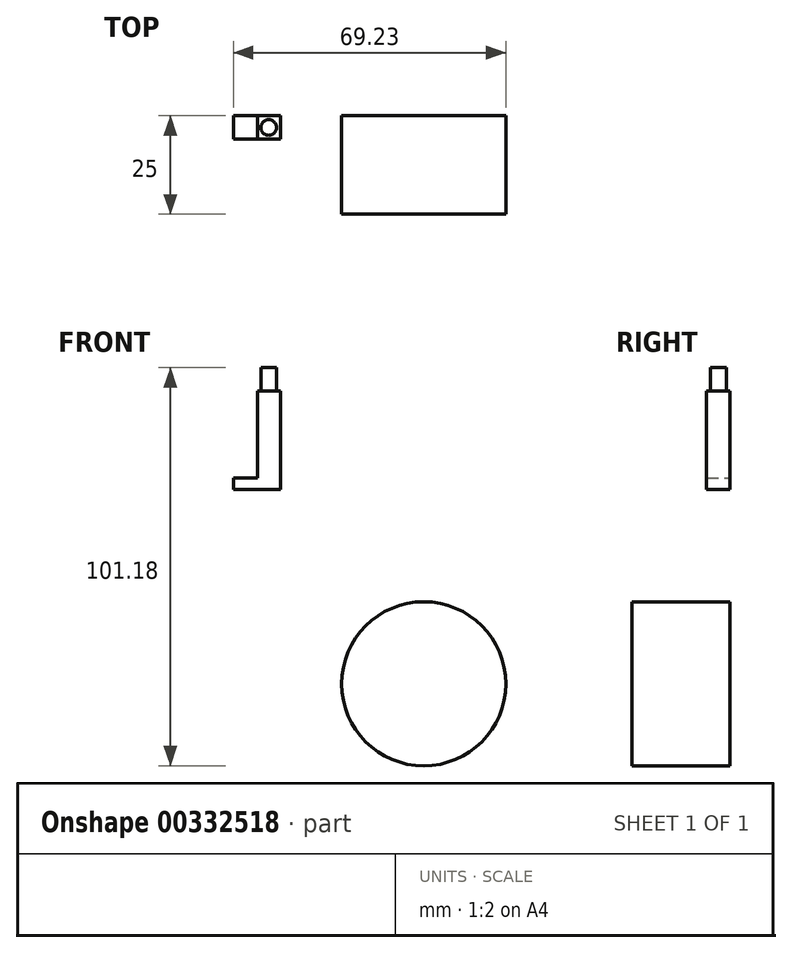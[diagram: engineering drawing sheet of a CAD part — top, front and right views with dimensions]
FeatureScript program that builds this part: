
annotation { "Feature Type Name" : "Feature", "Feature Type Description" : "" }
export const myFeature = defineFeature(function(context is Context, id is Id, definition is map)
    precondition{}
    {
        {
            var Q0;
            Q0=qCreatedBy(makeId("Front.planeOp"),FACE);
            var sketch = newSketch(context, id + "F0", { "sketchPlane" : qUnion([Q0])});
            skCircle(sketch, "E0", {"center": v(0, 0) * mm, "radius": 20.84 * mm});
            skSolve(sketch);
        }
        {
            var Q0;
            Q0 = qSketchRegion(id + "F0", true);
            extrude(context, id + "F1", {"entities" : qUnion([Q0]), "depth" : 25 * mm});
        }
        {
            var Q0;
            Q0=qCreatedBy(makeId("Front.planeOp"),FACE);
            var sketch = newSketch(context, id + "F2", { "sketchPlane" : qUnion([Q0])});
            skLineSegment(sketch, "E1", {"start": v(-47.44, 33.57) * mm, "end": v(-47.44, 31.07) * mm});
            skLineSegment(sketch, "E2", {"start": v(-47.44, 31.07) * mm, "end": v(3.32, 13.52) * mm});
            skLineSegment(sketch, "E3", {"start": v(-36.39, 74.34) * mm, "end": v(-36.39, 49.34) * mm});
            skLineSegment(sketch, "E4", {"start": v(-36.39, 49.34) * mm, "end": v(-48.39, 49.34) * mm});
            skLineSegment(sketch, "E5", {"start": v(-48.39, 49.34) * mm, "end": v(-48.39, 52.34) * mm});
            skLineSegment(sketch, "E6", {"start": v(-48.39, 52.34) * mm, "end": v(-42.22, 52.34) * mm});
            skLineSegment(sketch, "E7", {"start": v(-42.22, 52.34) * mm, "end": v(-42.22, 74.34) * mm});
            skLineSegment(sketch, "E8", {"start": v(-42.22, 74.34) * mm, "end": v(-36.39, 74.34) * mm});
            skSolve(sketch);
        }
        {
            var Q0;
            Q0 = qSketchRegion(id + "F2", true);
            extrude(context, id + "F3", {"entities" : qUnion([Q0]), "depth" : 6 * mm});
        }
        {
            var Q0;
            Q0=makeQuery(id+"F3.opExtrude","SWEPT_FACE",FACE,{"disambiguationData":[OSD([sQuery(id+"F2.wireOp",EDGE,"E8")])]});
            var sketch = newSketch(context, id + "F4", { "sketchPlane" : qUnion([Q0])});
            skCircle(sketch, "E9", {"center": v(-39.39, -3) * mm, "radius": 2 * mm});
            skSolve(sketch);
        }
        {
            var Q0;
            Q0 = qSketchRegion(id + "F4", true);
            extrude(context, id + "F5", {"entities" : qUnion([Q0]), "operationType" : NewBodyOperationType.ADD, "depth" : 6 * mm});
        }
    });
